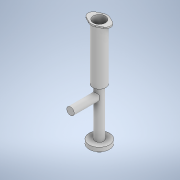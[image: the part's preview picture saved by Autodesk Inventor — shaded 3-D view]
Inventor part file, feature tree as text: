
AUTODESK INVENTOR PART (.ipt)
format: ipt  version: 2022 (Build 260153000, 153)  size: 169,984 bytes
history: native  units: mm
features: extrude x8, sketch x8, pattern_circular x1, projected_geometry x1
ambient origin geometry x8: Origin, YZ Plane, XZ Plane, XY Plane, X Axis, Y Axis, Z Axis, Center Point
bodies: Solid1 (feature_tree)
feature tree (18):
  extrude  "Extrusion1"  Depth=91.0mm TaperAngle=0.0deg
  extrude  "Extrusion2"  Depth=90.0mm TaperAngle=0.0deg
  extrude  "Extrusion3"  Depth=77.8mm TaperAngle=0.0deg
  extrude  "Extrusion4"  Depth=6.5mm TaperAngle=0.0deg
  extrude  "Extrusion5"  Depth=8.8mm TaperAngle=0.0deg
  extrude  "Extrusion6"  Depth=15.0mm
  extrude  "Extrusion7"  Depth=25.7mm
  pattern_circular  "Circular Pattern1"  [2 undecoded]
  extrude  "Extrusion8"  Depth=15.0mm
  sketch  "Sketch1"  dims[d0=21.3mm d1=91.0mm d2=0.0mm]
  sketch  "Sketch2"  dims[d3=19.8mm d4=90.0mm d5=0.0mm]
  sketch  "Sketch3"  dims[d6=13.5mm d7=77.8mm d8=0.0mm]
  sketch  "Sketch4"  dims[d9=33.2mm d10=6.5mm d11=0.0mm]
  sketch  "Sketch5"  dims[d12=9.9mm d13=8.8mm d14=0.0mm]
  sketch  "Sketch6"  dims[d15=15.0mm d16=12.2mm]
  sketch  "Sketch7"  dims[d17=47.0mm d18=0.0mm d19=25.7mm]
  sketch  "Sketch8"  dims[d20=2.2mm d21=0.0mm d22=8.5mm d23=15.0mm d24=20.0mm d25=90.0deg d27=2.2mm d28=0.0mm]
  projected_geometry  "Projected Loop1"
note: 2 required parameter values undecoded (feature->parameter linkage not recoverable at this tier; creation-order binding heuristic only, values carry confidence <= 0.55)
